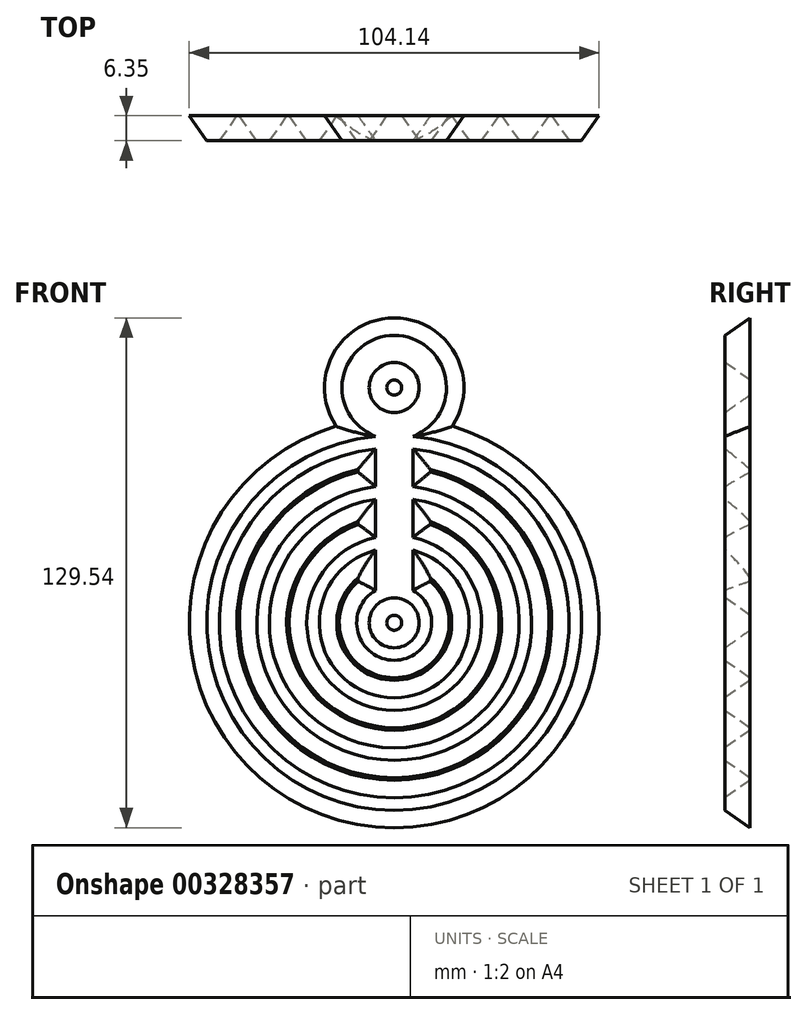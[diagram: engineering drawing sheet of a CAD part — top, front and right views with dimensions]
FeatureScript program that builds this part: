
annotation { "Feature Type Name" : "Feature", "Feature Type Description" : "" }
export const myFeature = defineFeature(function(context is Context, id is Id, definition is map)
    precondition{}
    {
        {
            var Q0;
            Q0=qCreatedBy(makeId("Front.planeOp"),FACE);
            var sketch = newSketch(context, id + "F0", { "sketchPlane" : qUnion([Q0])});
            skCircle(sketch, "E0", {"center": v(0, 0) * mm, "radius": 6.35 * mm});
            skCircle(sketch, "E1", {"center": v(0, 0) * mm, "radius": 9.53 * mm});
            skCircle(sketch, "E2", {"center": v(0, 0) * mm, "radius": 19.05 * mm});
            skCircle(sketch, "E3", {"center": v(0, 0) * mm, "radius": 22.23 * mm});
            skCircle(sketch, "E4", {"center": v(0, 0) * mm, "radius": 31.75 * mm});
            skCircle(sketch, "E5", {"center": v(0, 0) * mm, "radius": 34.93 * mm});
            skCircle(sketch, "E6", {"center": v(0, 0) * mm, "radius": 44.45 * mm});
            skCircle(sketch, "E7", {"center": v(0, 0) * mm, "radius": 47.63 * mm});
            skLineSegment(sketch, "E8", {"start": v(-4.76, 8.25) * mm, "end": v(-4.76, 18.45) * mm});
            skLineSegment(sketch, "E9", {"start": v(4.76, 8.25) * mm, "end": v(4.76, 18.45) * mm});
            skLineSegment(sketch, "E10.trimOffspring", {"start": v(-4.76, 34.6) * mm, "end": v(-4.76, 44.2) * mm});
            skLineSegment(sketch, "E11.trimOffspring", {"start": v(4.76, 34.6) * mm, "end": v(4.76, 44.2) * mm});
            skLineSegment(sketch, "E12.trimOffspring", {"start": v(-4.76, 21.7) * mm, "end": v(-4.76, 31.4) * mm});
            skLineSegment(sketch, "E13.trimOffspring", {"start": v(4.76, 21.71) * mm, "end": v(4.76, 31.4) * mm});
            skArc(sketch, "E14", {"start": v(4.76, 47.39) * mm, "mid": v(0, 73.03) * mm, "end": v(-4.76, 47.39) * mm});
            skCircle(sketch, "E15", {"center": v(0, 59.76) * mm, "radius": 6.35 * mm});
            skSolve(sketch);
        }
        {
            var Q0;
            {var subQ0=sQuery(id+"F0.wireOp",EDGE,"E14");Q0=makeQuery(id+"F0.imprint","IMPRINT",FACE,{"disambiguationData":[TD([[makeQuery(id+"F0.imprint","IMPRINT",EDGE,{"derivedFrom":subQ0}),1.0]])]});}
            var Q1;
            {var subQ0=sQuery(id+"F0.wireOp",EDGE,"E6");var subQ1=makeQuery(id+"F0.imprint","INTERSECT",VERTEX,{"derivedFrom":[subQ0,sQuery(id+"F0.wireOp",EDGE,"E10.trimOffspring")]});Q1=makeQuery(id+"F0.imprint","IMPRINT",FACE,{"disambiguationData":[TD([[makeQuery(id+"F0.imprint","IMPRINT",EDGE,{"disambiguationData":[TD([[subQ1,1.0]])],"derivedFrom":subQ0}),-1.0]])]});}
            var Q2;
            {var subQ0=sQuery(id+"F0.wireOp",EDGE,"E10.trimOffspring");Q2=makeQuery(id+"F0.imprint","IMPRINT",FACE,{"disambiguationData":[TD([[makeQuery(id+"F0.imprint","IMPRINT",EDGE,{"derivedFrom":subQ0}),-1.0]])]});}
            var Q3;
            {var subQ0=sQuery(id+"F0.wireOp",EDGE,"E12.trimOffspring");Q3=makeQuery(id+"F0.imprint","IMPRINT",FACE,{"disambiguationData":[TD([[makeQuery(id+"F0.imprint","IMPRINT",EDGE,{"derivedFrom":subQ0}),-1.0]])]});}
            var Q4;
            {var subQ0=sQuery(id+"F0.wireOp",EDGE,"E4");var subQ1=makeQuery(id+"F0.imprint","INTERSECT",VERTEX,{"derivedFrom":[subQ0,sQuery(id+"F0.wireOp",EDGE,"E12.trimOffspring")]});Q4=makeQuery(id+"F0.imprint","IMPRINT",FACE,{"disambiguationData":[TD([[makeQuery(id+"F0.imprint","IMPRINT",EDGE,{"disambiguationData":[TD([[subQ1,1.0]])],"derivedFrom":subQ0}),-1.0]])]});}
            var Q5;
            {var subQ0=sQuery(id+"F0.wireOp",EDGE,"E8");Q5=makeQuery(id+"F0.imprint","IMPRINT",FACE,{"disambiguationData":[TD([[makeQuery(id+"F0.imprint","IMPRINT",EDGE,{"derivedFrom":subQ0}),-1.0]])]});}
            var Q6;
            {var subQ0=sQuery(id+"F0.wireOp",EDGE,"E2");var subQ1=makeQuery(id+"F0.imprint","INTERSECT",VERTEX,{"derivedFrom":[subQ0,sQuery(id+"F0.wireOp",EDGE,"E8")]});Q6=makeQuery(id+"F0.imprint","IMPRINT",FACE,{"disambiguationData":[TD([[makeQuery(id+"F0.imprint","IMPRINT",EDGE,{"disambiguationData":[TD([[subQ1,1.0]])],"derivedFrom":subQ0}),-1.0]])]});}
            var Q7;
            Q7=makeQuery(id+"F0.imprint","IMPRINT",FACE,{"disambiguationData":[TD([[makeQuery(id+"F0.imprint","IMPRINT",EDGE,{"derivedFrom":sQuery(id+"F0.wireOp",EDGE,"E0")}),-1.0]])]});
            extrude(context, id + "F1", {"entities" : qUnion([Q0, Q1, Q2, Q3, Q4, Q5, Q6, Q7]), "oppositeDirection" : true, "depth" : 6.35 * mm, "hasDraft" : true, "draftAngle" : 35 * degree});
        }
    });
